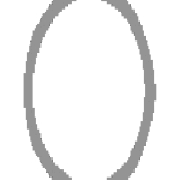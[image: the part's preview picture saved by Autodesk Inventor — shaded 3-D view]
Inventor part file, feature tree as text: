
AUTODESK INVENTOR PART (.ipt)
format: ipt  version: 2021 (Build 250183000, 183)  size: 114,176 bytes
history: native  units: in
note: dims shown in document units (in); Inventor stores cm internally (conversion verified against a paired STEP export)
features: other x4, sketch x3, plane x1
ambient origin geometry x8: Origin, YZ Plane, XZ Plane, XY Plane, X Axis, Y Axis, Z Axis, Center Point
bodies: Solid1 (feature_tree), Body (feature_tree)
feature tree (8):
  other  "Driven Length"
  other  "Frame Generator"
  other  "Start Plane"
  other  "End Plane"
  sketch  "Sketch"  dims[d2=2.0in d4=-0.0in d5=2.0in d6=0.12in d7=0.0in d8=90.0deg d9=2.0in]
  sketch  "Sketch2"  dims[d0=1.0in]
  plane  "Work Plane3"
  sketch  "Sketch3"  dims[d1=0.065in]
